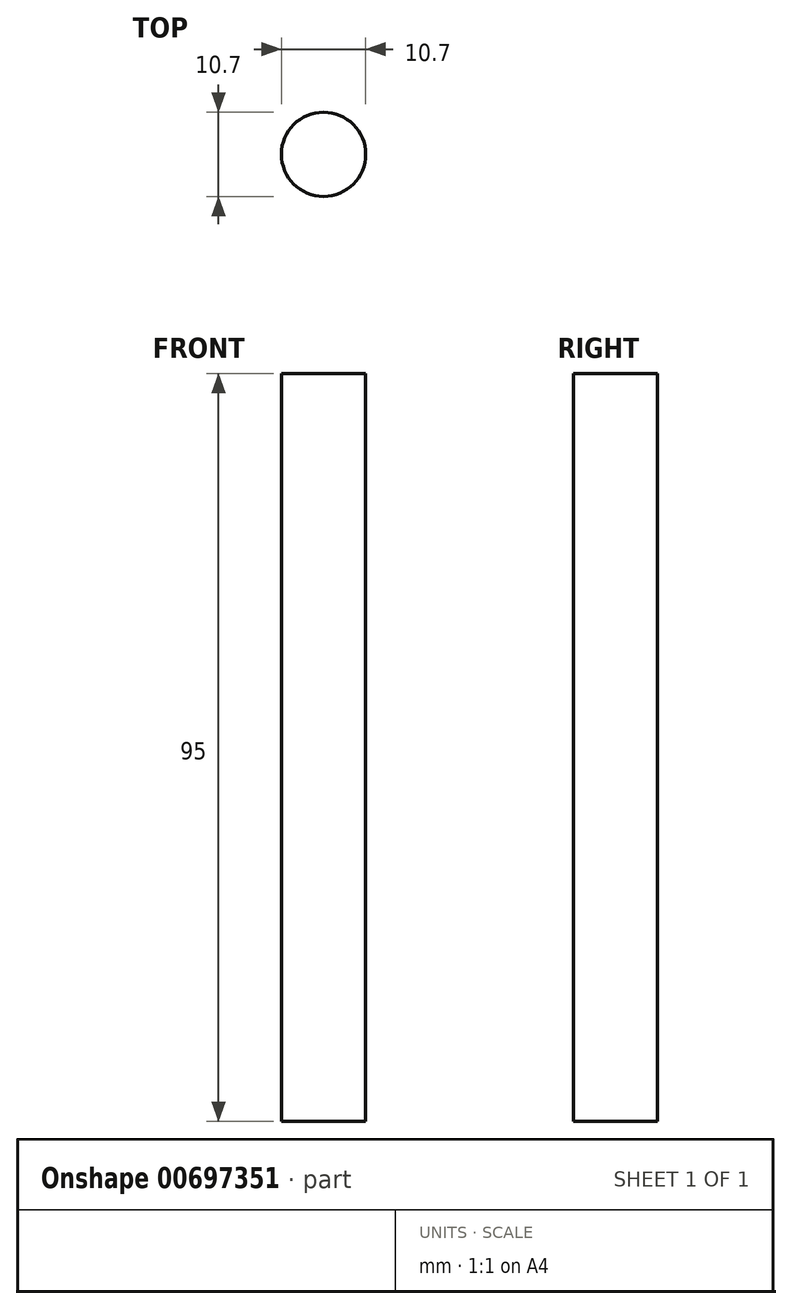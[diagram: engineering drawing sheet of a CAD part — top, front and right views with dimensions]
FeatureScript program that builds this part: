
annotation { "Feature Type Name" : "Feature", "Feature Type Description" : "" }
export const myFeature = defineFeature(function(context is Context, id is Id, definition is map)
    precondition{}
    {
        {
            var Q0;
            Q0=qCreatedBy(makeId("Top.planeOp"),FACE);
            var sketch = newSketch(context, id + "F0", { "sketchPlane" : qUnion([Q0])});
            skCircle(sketch, "E0", {"center": v(0, 0) * mm, "radius": 5.35 * mm});
            skSolve(sketch);
        }
        {
            var Q0;
            Q0 = qSketchRegion(id + "F0", true);
            extrude(context, id + "F1", {"entities" : qUnion([Q0]), "depth" : 95 * mm, "offsetDistance" : 25 * mm});
        }
    });
